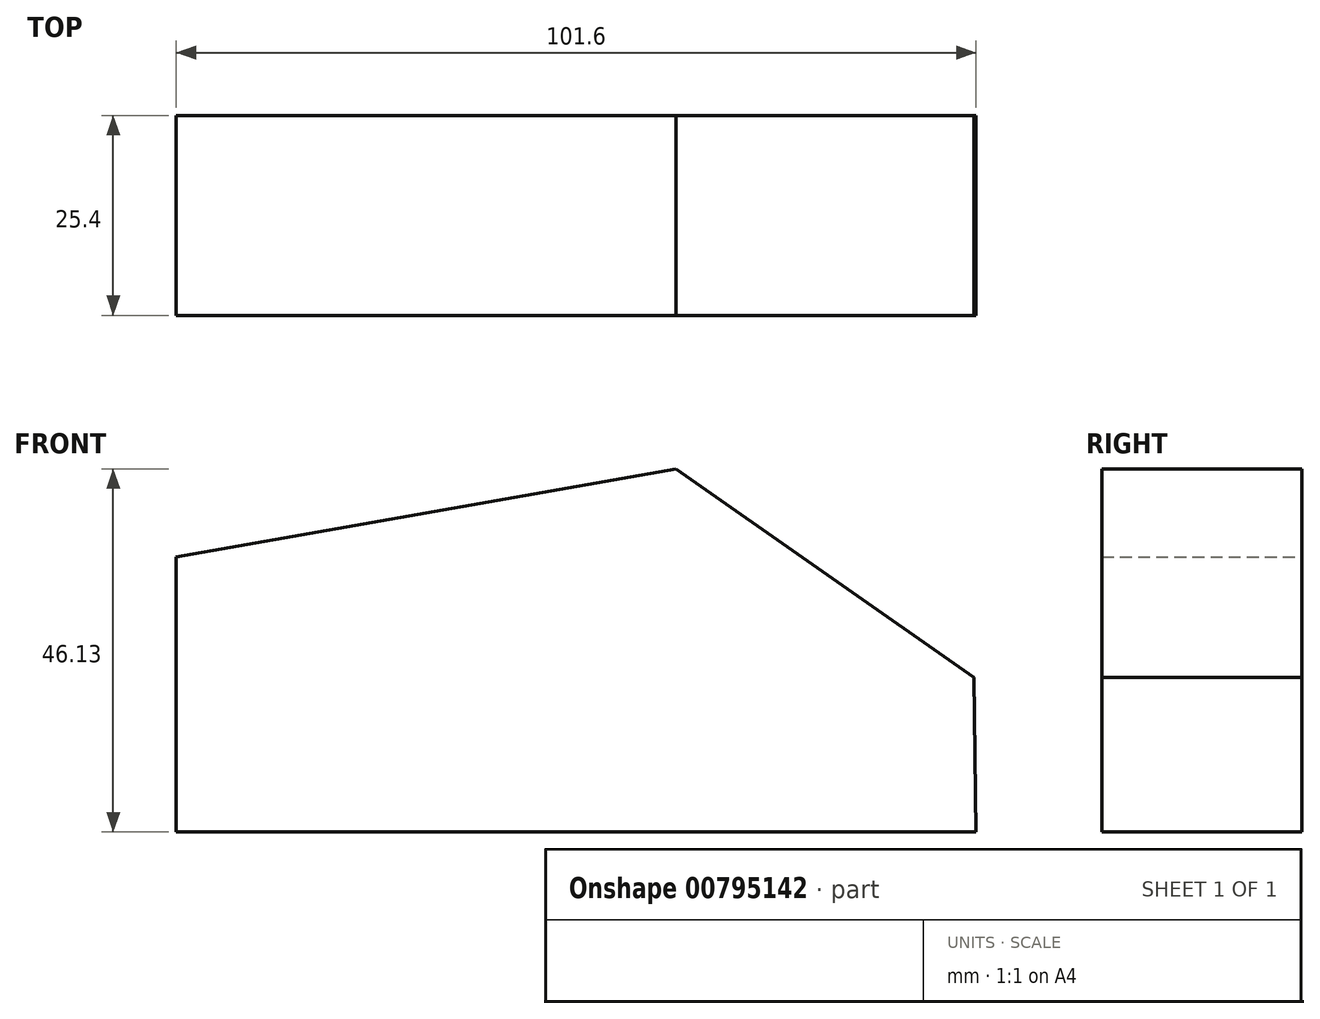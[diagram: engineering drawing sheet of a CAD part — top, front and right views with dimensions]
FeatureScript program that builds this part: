
annotation { "Feature Type Name" : "Feature", "Feature Type Description" : "" }
export const myFeature = defineFeature(function(context is Context, id is Id, definition is map)
    precondition{}
    {
        {
            var Q0;
            Q0=qCreatedBy(makeId("Front.planeOp"),FACE);
            var sketch = newSketch(context, id + "F0", { "sketchPlane" : qUnion([Q0])});
            skLineSegment(sketch, "E0", {"start": v(-50.67, 25.1) * mm, "end": v(-50.67, -9.82) * mm});
            skLineSegment(sketch, "E1", {"start": v(-50.67, 25.1) * mm, "end": v(12.83, 36.3) * mm});
            skLineSegment(sketch, "E2", {"start": v(-50.67, -9.82) * mm, "end": v(50.93, -9.82) * mm});
            skLineSegment(sketch, "E3", {"start": v(12.83, 36.3) * mm, "end": v(50.67, 9.82) * mm});
            skLineSegment(sketch, "E4", {"start": v(50.67, 9.82) * mm, "end": v(50.93, -9.82) * mm});
            skLineSegment(sketch, "E5", {"start": v(-50.67, -9.82) * mm, "end": v(50.67, 9.82) * mm, "construction": true});
            skPoint(sketch, "E6", {"position": v(0, 22.85) * mm});
            skPoint(sketch, "E6.positionSnap0", {"position": v(0, 0) * mm});
            skSolve(sketch);
        }
        {
            var Q0;
            Q0=makeQuery(id+"F0.imprint","IMPRINT",FACE,{"disambiguationData":[TD([[makeQuery(id+"F0.imprint","IMPRINT",EDGE,{"derivedFrom":sQuery(id+"F0.wireOp",EDGE,"E0")}),1.0]])]});
            extrude(context, id + "F1", {"entities" : qUnion([Q0]), "endBound" : BoundingType.SYMMETRIC, "depth" : 25.4 * mm, "offsetDistance" : 25.4 * mm});
        }
    });
